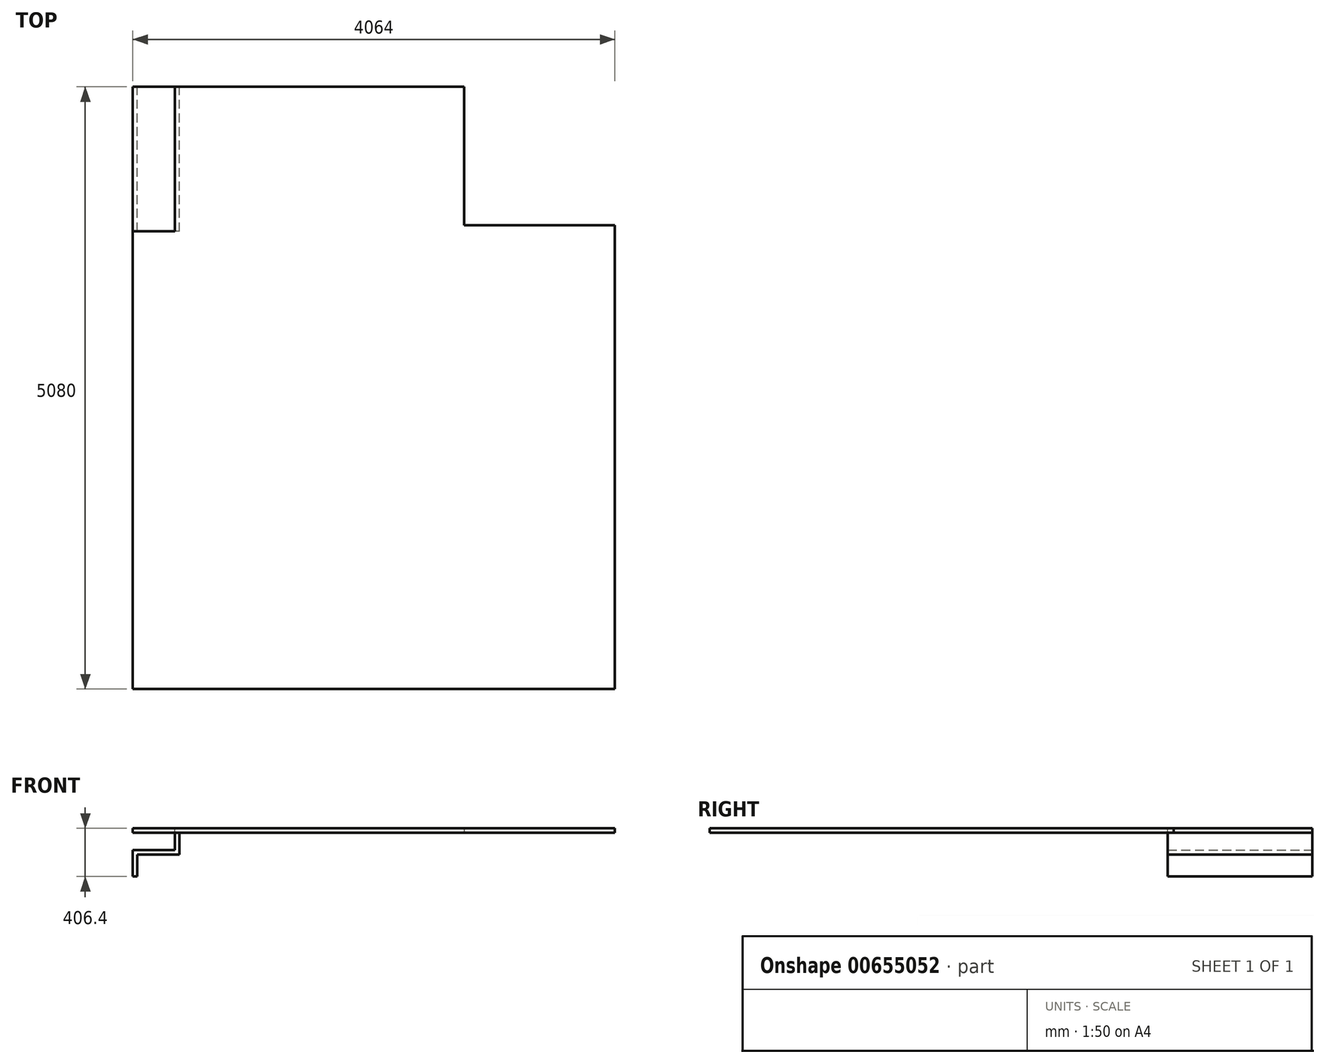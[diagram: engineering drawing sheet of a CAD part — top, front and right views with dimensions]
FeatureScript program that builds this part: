
annotation { "Feature Type Name" : "Feature", "Feature Type Description" : "" }
export const myFeature = defineFeature(function(context is Context, id is Id, definition is map)
    precondition{}
    {
        {
            var Q0;
            Q0=qCreatedBy(makeId("Top.planeOp"),FACE);
            var sketch = newSketch(context, id + "F0", { "sketchPlane" : qUnion([Q0])});
            skLineSegment(sketch, "E0", {"start": v(0, 0) * mm, "end": v(0, -5080) * mm});
            skLineSegment(sketch, "E1", {"start": v(0, -5080) * mm, "end": v(4064, -5080) * mm});
            skLineSegment(sketch, "E2", {"start": v(4064, -5080) * mm, "end": v(4064, -1168.4) * mm});
            skLineSegment(sketch, "E3", {"start": v(4064, -1168.4) * mm, "end": v(2794, -1168.4) * mm});
            skLineSegment(sketch, "E4", {"start": v(2794, -1168.4) * mm, "end": v(2794, 0) * mm});
            skLineSegment(sketch, "E5", {"start": v(2794, 0) * mm, "end": v(0, 0) * mm});
            skSolve(sketch);
        }
        {
            var Q0;
            Q0=makeQuery(id+"F0.imprint","IMPRINT",FACE,{"disambiguationData":[TD([[makeQuery(id+"F0.imprint","IMPRINT",EDGE,{"derivedFrom":sQuery(id+"F0.wireOp",EDGE,"E0")}),1.0]])]});
            extrude(context, id + "F1", {"entities" : qUnion([Q0]), "depth" : 38.1 * mm, "offsetDistance" : 25.4 * mm});
        }
        {
            var Q0;
            Q0=makeQuery(id+"F1.opExtrude","CAP_FACE",FACE,{"disambiguationData":[OSD([sQuery(id+"F0.wireOp",EDGE,"E0"),sQuery(id+"F0.wireOp",EDGE,"E1"),sQuery(id+"F0.wireOp",EDGE,"E2"),sQuery(id+"F0.wireOp",EDGE,"E3"),sQuery(id+"F0.wireOp",EDGE,"E4"),sQuery(id+"F0.wireOp",EDGE,"E5")])],"isStart":false});
            var sketch = newSketch(context, id + "F2", { "sketchPlane" : qUnion([Q0])});
            skLineSegment(sketch, "E6.bottom", {"start": v(0, 0) * mm, "end": v(355.6, 0) * mm});
            skLineSegment(sketch, "E6.top", {"start": v(0, -1219.2) * mm, "end": v(355.6, -1219.2) * mm});
            skLineSegment(sketch, "E6.left", {"start": v(0, 0) * mm, "end": v(0, -1219.2) * mm});
            skLineSegment(sketch, "E6.right", {"start": v(355.6, 0) * mm, "end": v(355.6, -1219.2) * mm});
            skSolve(sketch);
        }
        {
            var Q0;
            Q0=makeQuery(id+"F2.imprint","IMPRINT",FACE,{"disambiguationData":[TD([[makeQuery(id+"F2.imprint","IMPRINT",EDGE,{"derivedFrom":sQuery(id+"F2.wireOp",EDGE,"E6.bottom")}),1.0]])]});
            extrude(context, id + "F3", {"entities" : qUnion([Q0]), "operationType" : NewBodyOperationType.REMOVE, "oppositeDirection" : true, "depth" : 38.1 * mm, "offsetDistance" : 25.4 * mm});
        }
        {
            var Q0;
            Q0=makeQuery(id+"F1.opExtrude","SWEPT_FACE",FACE,{"disambiguationData":[OSD([sQuery(id+"F0.wireOp",EDGE,"E5")])]});
            var sketch = newSketch(context, id + "F4", { "sketchPlane" : qUnion([Q0])});
            skLineSegment(sketch, "E7", {"start": v(-355.6, 0) * mm, "end": v(-393.7, 0) * mm});
            skLineSegment(sketch, "E8", {"start": v(-393.7, 0) * mm, "end": v(-393.7, -184.15) * mm});
            skLineSegment(sketch, "E9", {"start": v(-393.7, -184.15) * mm, "end": v(-38.1, -184.15) * mm});
            skLineSegment(sketch, "E10", {"start": v(-38.1, -184.15) * mm, "end": v(-38.1, -368.3) * mm});
            skLineSegment(sketch, "E11", {"start": v(-38.1, -368.3) * mm, "end": v(0, -368.3) * mm});
            skLineSegment(sketch, "E12", {"start": v(0, -368.3) * mm, "end": v(0, -146.05) * mm});
            skLineSegment(sketch, "E13", {"start": v(0, -146.05) * mm, "end": v(-317.5, -146.05) * mm});
            skLineSegment(sketch, "E14", {"start": v(-317.5, -146.05) * mm, "end": v(-355.6, -146.05) * mm});
            skLineSegment(sketch, "E15", {"start": v(-355.6, -146.05) * mm, "end": v(-355.6, 0) * mm});
            skSolve(sketch);
        }
        {
            var Q0;
            Q0=makeQuery(id+"F4.imprint","IMPRINT",FACE,{"disambiguationData":[TD([[makeQuery(id+"F4.imprint","IMPRINT",EDGE,{"derivedFrom":sQuery(id+"F4.wireOp",EDGE,"E7")}),-1.0]])]});
            extrude(context, id + "F5", {"entities" : qUnion([Q0]), "operationType" : NewBodyOperationType.ADD, "oppositeDirection" : true, "depth" : 1219.2 * mm, "offsetDistance" : 25.4 * mm});
        }
    });
